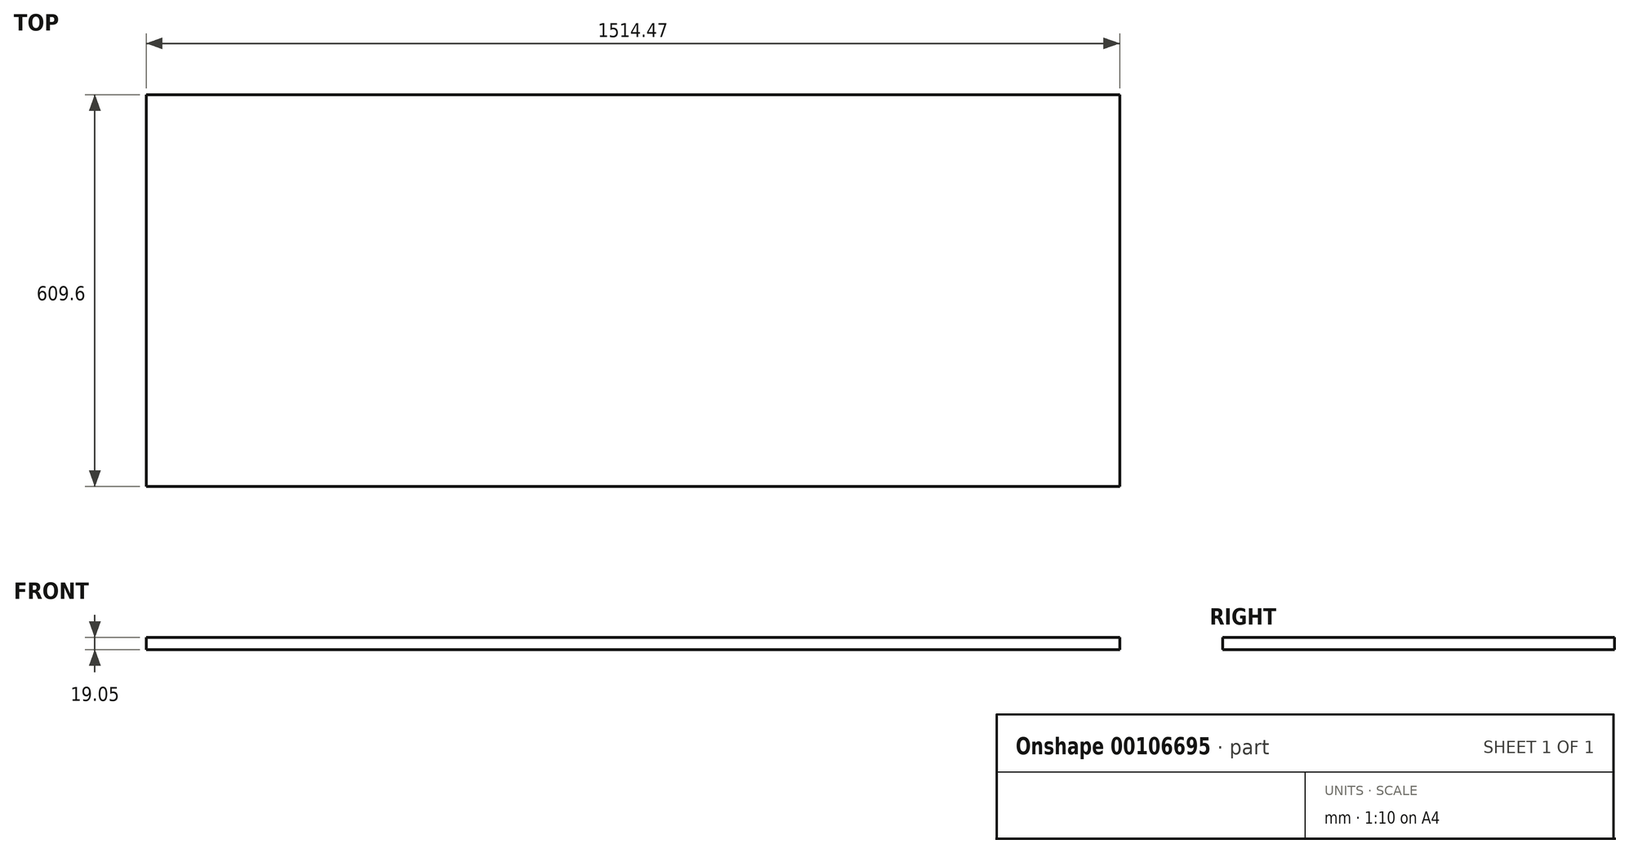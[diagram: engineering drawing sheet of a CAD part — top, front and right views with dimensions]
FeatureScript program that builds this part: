
annotation { "Feature Type Name" : "Feature", "Feature Type Description" : "" }
export const myFeature = defineFeature(function(context is Context, id is Id, definition is map)
    precondition{}
    {
        {
            var Q0;
            Q0=qCreatedBy(makeId("Top.planeOp"),FACE);
            var sketch = newSketch(context, id + "F0", { "sketchPlane" : qUnion([Q0])});
            skLineSegment(sketch, "E0.bottom", {"start": v(0, 0) * mm, "end": v(1514.47, 0) * mm});
            skLineSegment(sketch, "E0.top", {"start": v(0, 609.6) * mm, "end": v(1514.47, 609.6) * mm});
            skLineSegment(sketch, "E0.left", {"start": v(0, 0) * mm, "end": v(0, 609.6) * mm});
            skLineSegment(sketch, "E0.right", {"start": v(1514.47, 0) * mm, "end": v(1514.47, 609.6) * mm});
            skSolve(sketch);
        }
        {
            var Q0;
            Q0=makeQuery(id+"F0.imprint","IMPRINT",FACE,{"disambiguationData":[TD([[makeQuery(id+"F0.imprint","IMPRINT",EDGE,{"derivedFrom":sQuery(id+"F0.wireOp",EDGE,"E0.bottom")}),1.0]])]});
            extrude(context, id + "F1", {"entities" : qUnion([Q0]), "depth" : 19.05 * mm});
        }
    });
